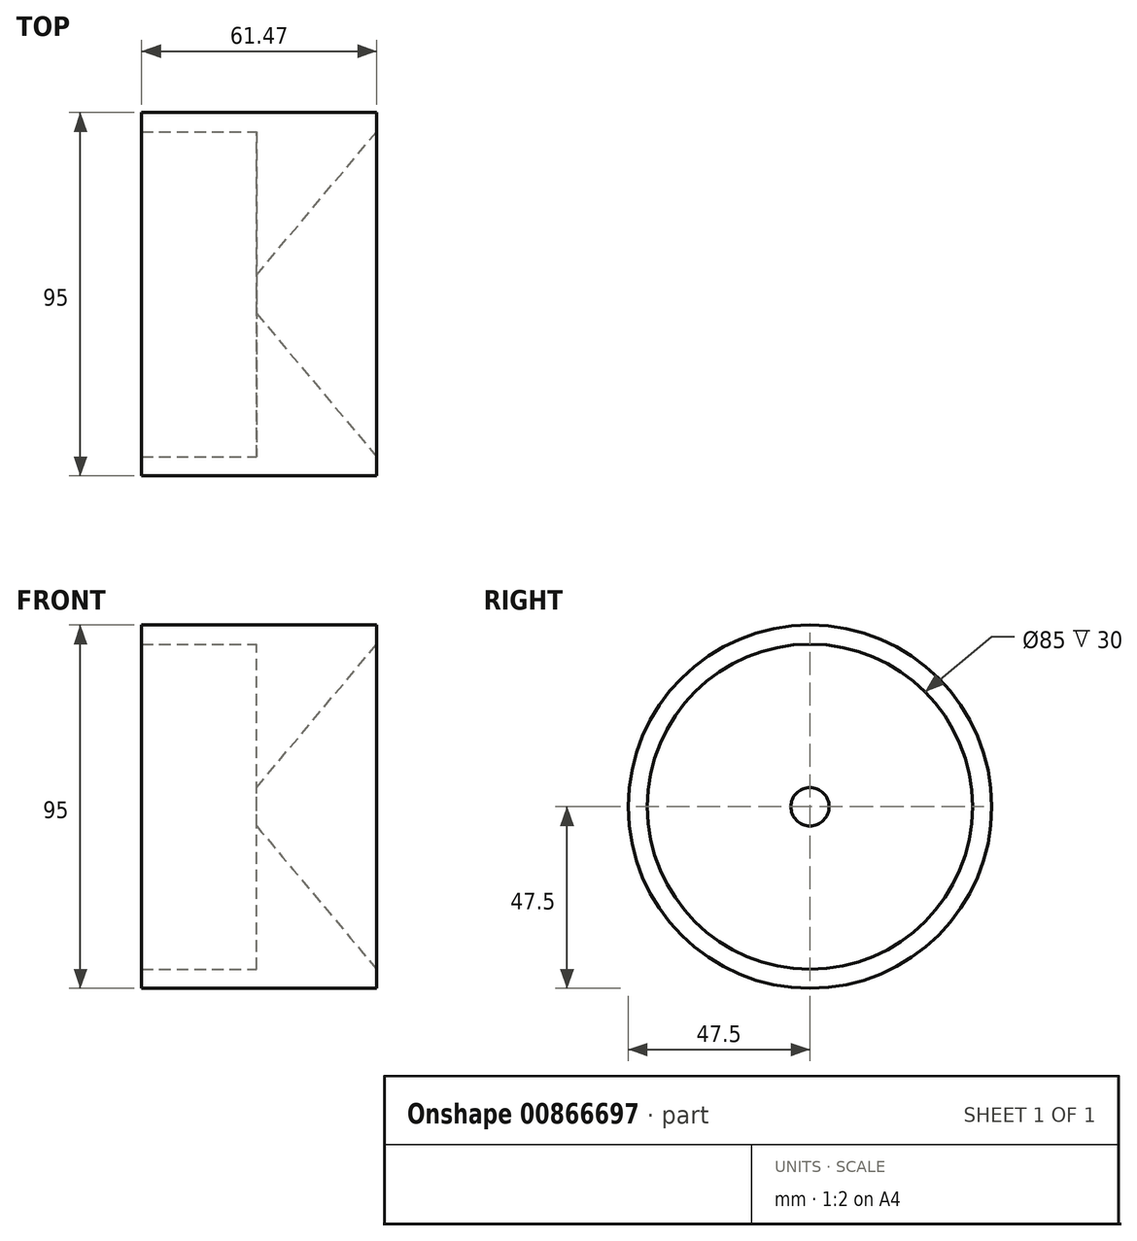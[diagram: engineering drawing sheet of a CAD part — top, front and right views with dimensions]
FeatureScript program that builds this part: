
annotation { "Feature Type Name" : "Feature", "Feature Type Description" : "" }
export const myFeature = defineFeature(function(context is Context, id is Id, definition is map)
    precondition{}
    {
        {
            var Q0;
            Q0=qCreatedBy(makeId("Front.planeOp"),FACE);
            var sketch = newSketch(context, id + "F0", { "sketchPlane" : qUnion([Q0])});
            skLineSegment(sketch, "E0", {"start": v(0, 0) * mm, "end": v(-61.47, 0) * mm, "construction": true});
            skLineSegment(sketch, "E1", {"start": v(-61.47, 42.5) * mm, "end": v(-61.47, 47.5) * mm});
            skLineSegment(sketch, "E2", {"start": v(-61.47, 47.5) * mm, "end": v(0, 47.5) * mm});
            skLineSegment(sketch, "E3", {"start": v(0, 47.5) * mm, "end": v(0, 42.5) * mm});
            skLineSegment(sketch, "E4", {"start": v(0, 42.5) * mm, "end": v(-31.47, 5) * mm});
            skLineSegment(sketch, "E5", {"start": v(-31.47, 5) * mm, "end": v(-31.47, 42.5) * mm});
            skLineSegment(sketch, "E6", {"start": v(-31.47, 42.5) * mm, "end": v(-61.47, 42.5) * mm});
            skSolve(sketch);
        }
        {
            var Q0;
            Q0=makeQuery(id+"F0.imprint","IMPRINT",FACE,{"disambiguationData":[TD([[makeQuery(id+"F0.imprint","IMPRINT",EDGE,{"derivedFrom":sQuery(id+"F0.wireOp",EDGE,"E1")}),-1.0]])]});
            var Q1;
            Q1=sQuery(id+"F0.wireOp",EDGE,"E0");
            revolve(context, id + "F1", {"surfaceOperationType" : NewSurfaceOperationType.NEW, "entities" : qUnion([Q0]), "axis" : qUnion([Q1]), "revolveType" : RevolveType.FULL});
        }
    });
